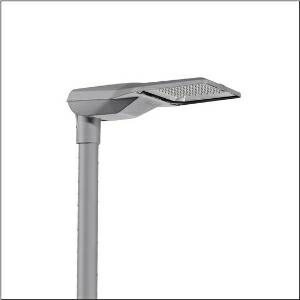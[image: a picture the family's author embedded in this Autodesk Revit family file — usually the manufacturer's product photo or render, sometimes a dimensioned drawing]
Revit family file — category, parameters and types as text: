
# Revit family: streetlight_sl_21_iq_midi___st1_0a_5xe3d41g08mb_322d
name_source: partatom
category: Lighting Fixtures
units: mm (PartAtom-declared; Revit-internal decimal feet)

## family parameters
Cut with Voids When Loaded = No
Host = Face
Light Source = No
Part Type = Normal
Room Calculation Point = No
Round Connector Dimension = Use Diameter
Shared = No

## types (1)
- --- (1 x LED, 20360 lm, 146.7 W, 4000K)
    Apparent Load = 147 VA
    CIE Flux Codes = 37 72 97 100 100
    Color Rendering = 70
    Color Temperature = 4000K
    Default Elevation = 1800 mm
    Description = Streetlight SL 21 iQ midi, mast luminaire, primary light control with lens, of PMMA, primary optical cover: cover, of toughened safety glass, transparent, light distribution: ST1.0a, light emission: direct distribution, primary light characteristic: asymmetric, installation type: post-top, side-entry, LED, High Power LED, rated luminous flux: 20.360lm, luminous efficacy: 139lm/W, light colour: 740, colour temperature: 4000K, control gear: iQ Street-Remote, control: Street-Remote, Auto-Match, Temp-Guard, Lumen-Switch, Night-Set, Smart-Wire, Light-Fading, Desk-Remote (wireless, voltage-free reading and setting of iQ features in the workshop via application-optimized NFC function/RFID function), optimised constant luminous flux control (CLO 2.0), pre-setting: linear dimming characteristic, mains connection: 230..240V, AC, 50/60Hz, start of lifetime: 147W, end of service life: 161W, reduction: 62W, luminaire housing, of diecast aluminium, powder-coated, Siteco® metallic grey (DB 702S), corrosivity category C5 mid according to DIN EN ISO 12944, please order mast flange separately, inclination adjustable: 0°, 5°, 10°, 15°, sealing non-destructively replaceable, multi-level sealing system, length: 644mm, width: 335mm, height: 110mm, mast flange for spigot size: 42mm (side-entry): 5XC10008XM4, 60/48mm (side-entry/post-top): 5XC10108XM2, 76/60mm (side-entry/post-top): 5XC10108XM1, mounting height: 4..8m, protection rating (complete): IP66, insulation class (complete): insulation class II (safety insulation), certification: CE, ENEC, ENEC+, VDE, impact resistance: IK10, permissible operating ambient temperature for outdoor applications: -40..+50°C, standard-compliant lighting for roads and squares, packaging unit: 1 piece

Light Distribution: ST1.0a
    Height = 111 mm
    Lamp = 1 x LED
    Lamp Light Flux = 20360 lm
    Lamp Power = 146.7 W
    Lamp count = 1
    Length = 644 mm
    Luminous efficacy = 139 lm/W
    Manufacturer = Siteco
    ModVariant = No
    Model = 5XE3D41G08MB
    Number of Poles = 1
    OnlyDefault = Yes
    Power Factor = 1
    Product Name = Streetlight SL 21 iQ midi | ST1.0a
    Product group = mast luminaire | pylon top
    ProductGroupID = 6100
    Protection Class = Protection class II
    Protection Degree = IP 66
    RLX_Detail_Level = 1
    RLX_Emergency_Light_Flux = 0 lm
    RLX_Emergency_Type = 0
    RLX_Emergency_Type_DB = No
    RlxData = <blob elided: 26989 chars, md5=839bd66a>
    Socket = socket
    Standby Power = 0 W
    System Light Flux = 20360 lm
    System Power = 147 W
    Type Comments = factory setting: luminous flux: 100 % | dim-lin: 254 | 753 mA
    Type Image = l_1004298.jpg
    URL = http://relux.com
    VarID = @adj_189418
    Voltage = 0 V
    Weight = 0.00 kg
    Width = 336 mm

## geometry (parser evidence)
native form markers: Blend x4, Sweep x11
no freeform markers — native parametric forms only
